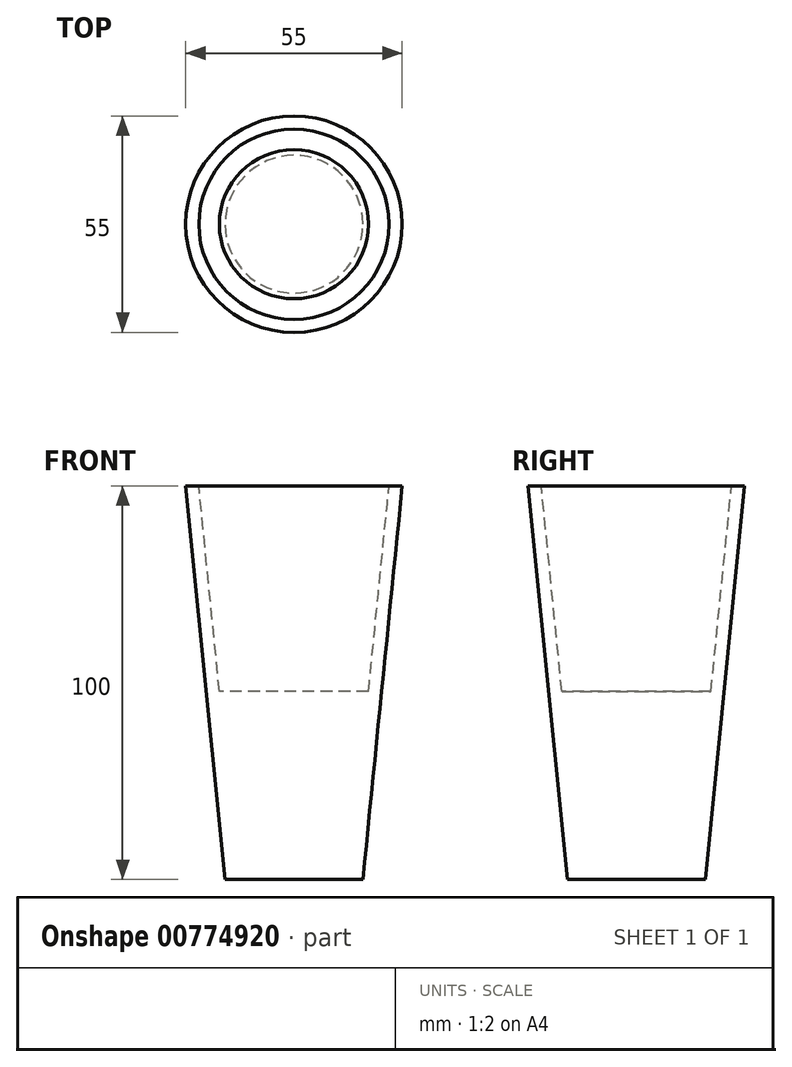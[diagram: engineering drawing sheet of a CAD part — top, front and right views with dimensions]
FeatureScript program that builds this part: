
annotation { "Feature Type Name" : "Feature", "Feature Type Description" : "" }
export const myFeature = defineFeature(function(context is Context, id is Id, definition is map)
    precondition{}
    {
        {
            var Q0;
            Q0=qCreatedBy(makeId("Front.planeOp"),FACE);
            var sketch = newSketch(context, id + "F0", { "sketchPlane" : qUnion([Q0])});
            skLineSegment(sketch, "E0", {"start": v(0, 0) * mm, "end": v(17.5, 0) * mm});
            skLineSegment(sketch, "E1", {"start": v(17.5, 0) * mm, "end": v(27.5, 100) * mm});
            skLineSegment(sketch, "E2", {"start": v(27.5, 100) * mm, "end": v(24.17, 100) * mm});
            skLineSegment(sketch, "E3", {"start": v(24.17, 100) * mm, "end": v(18.94, 47.76) * mm});
            skLineSegment(sketch, "E4", {"start": v(18.94, 47.76) * mm, "end": v(0, 47.76) * mm});
            skLineSegment(sketch, "E5", {"start": v(0, 47.76) * mm, "end": v(0, 0) * mm});
            skSolve(sketch);
        }
        {
            var Q0;
            Q0=makeQuery(id+"F0.imprint","IMPRINT",FACE,{"disambiguationData":[TD([[makeQuery(id+"F0.imprint","IMPRINT",EDGE,{"derivedFrom":sQuery(id+"F0.wireOp",EDGE,"E0")}),1.0]])]});
            var Q1;
            Q1=sQuery(id+"F0.wireOp",EDGE,"E5");
            revolve(context, id + "F1", {"surfaceOperationType" : NewSurfaceOperationType.NEW, "entities" : qUnion([Q0]), "axis" : qUnion([Q1]), "revolveType" : RevolveType.FULL});
        }
    });
